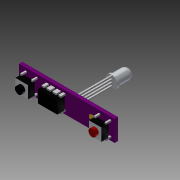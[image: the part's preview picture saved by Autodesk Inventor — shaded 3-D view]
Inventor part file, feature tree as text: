
AUTODESK INVENTOR PART (.ipt)
format: ipt  version: 2014 (Build 180170000, 170)  size: 440,320 bytes
history: native  units: in
note: dims shown in document units (in); Inventor stores cm internally (conversion verified against a paired STEP export)
features: extrude x17, sketch x17, projected_geometry x9, plane x3, hole x1, fillet x1
ambient origin geometry x8: Origin, YZ Plane, XZ Plane, XY Plane, X Axis, Y Axis, Z Axis, Center Point
bodies: Body1 (feature_tree)
feature tree (48):
  extrude  "Extrusion4"  Depth=0.4in
  plane  "Work Plane2"
  extrude  "Extrusion5"  Depth=0.06in
  extrude  "Extrusion6"  Depth=0.08in
  hole  "Hole1"  [1 undecoded]
  extrude  "Extrusion7"  Depth=0.14in
  extrude  "Extrusion8"  Depth=0.24in
  plane  "Work Plane3"
  extrude  "Extrusion10"  Depth=0.12in
  plane  "Work Plane4"
  extrude  "Extrusion11"  Depth=0.12in
  extrude  "Extrusion13"  Depth=0.24in
  fillet  "Fillet1"  Radius=0.24in
  extrude  "Extrusion14"  Depth=0.12in
  extrude  "Extrusion15"  Depth=0.14in
  extrude  "Extrusion16"  Depth=0.02in
  extrude  "Extrusion17"  Depth=0.24in
  extrude  "Extrusion18"  Depth=0.37in
  extrude  "Extrusion19"  Depth=0.725in
  extrude  "Extrusion20"  Depth=0.85in
  extrude  "Extrusion21"  Depth=0.001in
  extrude  "Extrusion22"  Depth=0.35in TaperAngle=0.0deg
  sketch  "Sketch4"  dims[d6=1.84in d7=0.4in]
  sketch  "Sketch6"  dims[d8=0.065in d9=0.0in d16=0.06in]
  projected_geometry  "Projected Loop1"
  sketch  "Sketch7"  dims[d17=0.24in d18=0.24in d22=0.08in]
  sketch  "Sketch8"  dims[d23=0.08in d24=0.065in]
  projected_geometry  "Projected Loop2"
  sketch  "Sketch9"  dims[d25=0.13in d26=0.0in d27=0.14in]
  sketch  "Sketch11"  dims[d28=0.12in d29=0.24in]
  projected_geometry  "Projected Loop4"
  projected_geometry  "Projected Loop5"
  sketch  "Sketch12"  dims[d30=0.24in d31=0.12in]
  projected_geometry  "Projected Loop6"
  sketch  "Sketch13"  dims[d32=0.06in d33=0.0in]
  projected_geometry  "Projected Loop7"
  sketch  "Sketch14"  dims[d34=0.2in d35=0.44in d36=0.115in d37=0.75in d38=0.375in d39=0.25in d40=0.5635in d41=1.0in d42=0.8108in d43=0.12in]
  sketch  "Sketch16"  dims[d44=0.08in d45=0.24in d46=0.24in]
  projected_geometry  "Projected Loop11"
  projected_geometry  "Projected Loop12"
  projected_geometry  "Projected Loop13"
  sketch  "Sketch17"  dims[d47=0.13in d48=0.0in d49=0.12in]
  sketch  "Sketch18"  dims[d50=0.12in d51=0.14in]
  sketch  "Sketch19"  dims[d52=0.06in d53=0.0in d54=0.02in]
  sketch  "Sketch20"  dims[d67=0.165in d68=0.24in]
  sketch  "Sketch21"  dims[d69=0.08in d70=0.37in]
  sketch  "Sketch22"  dims[d71=0.14in d72=0.0in d73=0.725in]
  sketch  "Sketch23"  dims[d74=0.2in d75=0.85in d76=0.2in d77=0.35in d78=0.0in d79=0.235in d82=0.04in d83=0.0in d84=0.1in d85=0.025in d88=0.0125in d89=0.01in d90=0.03in d91=0.03in d92=0.03in d93=0.04in d94=0.0in d95=0.03in d96=0.05in d97=0.075in d98=0.04in d99=0.04in d100=0.04in d101=0.1in d102=0.0in d103=0.001in d104=0.0in d105=0.001in d106=0.0in d107=0.001in d108=0.0in d109=0.001in d110=0.0in d111=0.03in d112=0.05in d113=0.075in d114=0.04in d115=0.04in d116=0.04in d117=0.08in d118=0.12in d119=0.24in d120=0.165in d121=0.36in d122=0.08in d123=0.24in d124=0.945in d125=0.09in d126=0.0in d127=0.001in d128=0.0in d129=0.001in d130=0.0in]
note: 1 required parameter value undecoded (feature->parameter linkage not recoverable at this tier; creation-order binding heuristic only, values carry confidence <= 0.55)
